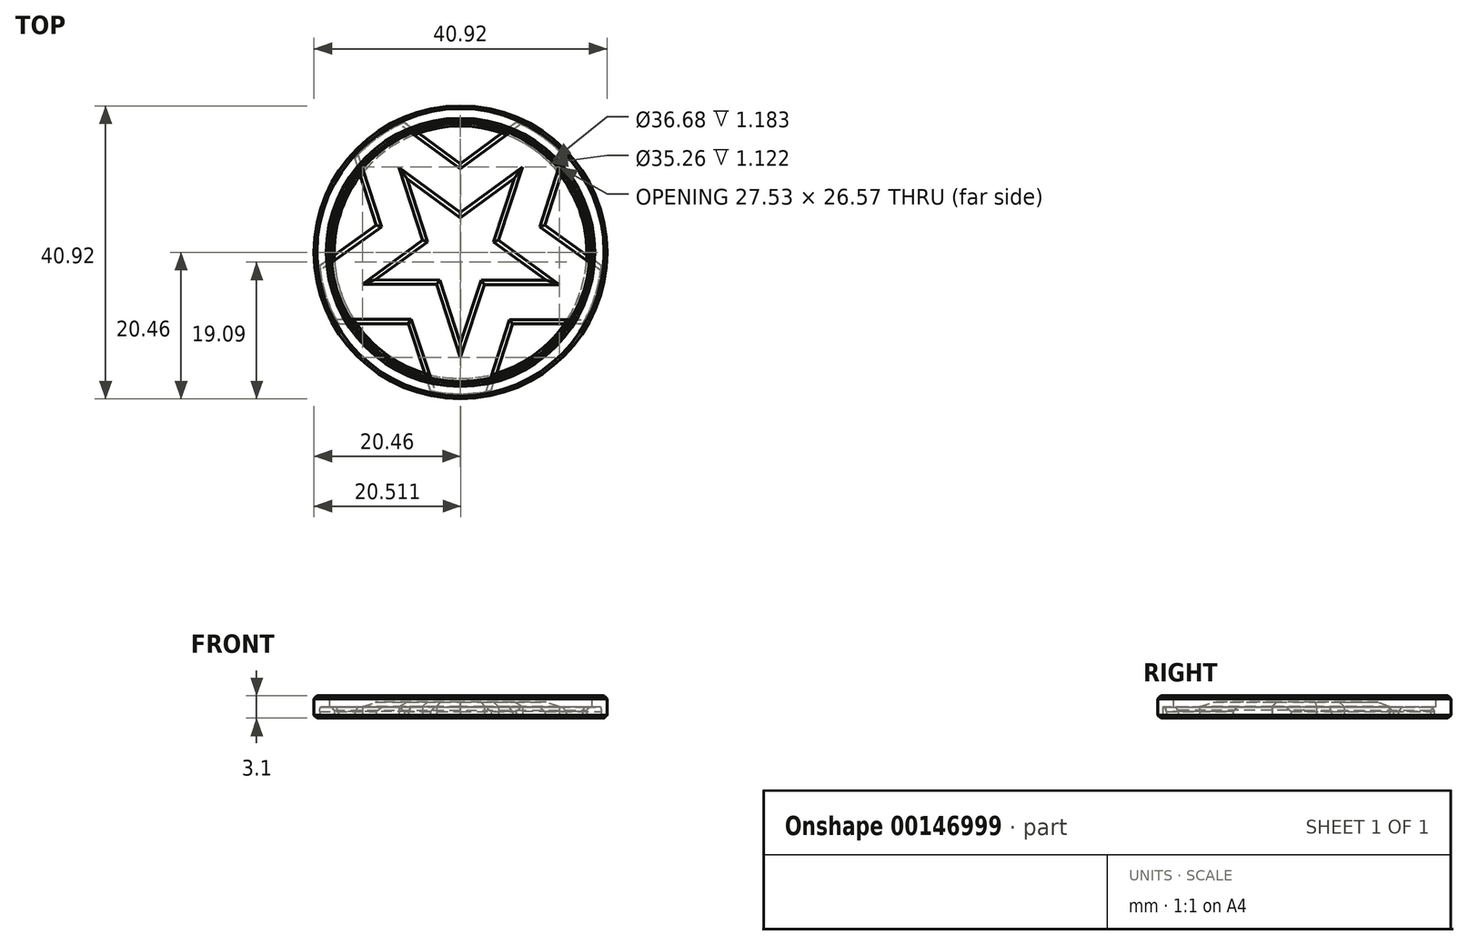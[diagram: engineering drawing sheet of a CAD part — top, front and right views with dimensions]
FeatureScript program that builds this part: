
annotation { "Feature Type Name" : "Feature", "Feature Type Description" : "" }
export const myFeature = defineFeature(function(context is Context, id is Id, definition is map)
    precondition{}
    {
        {
            var Q0;
            Q0=qCreatedBy(makeId("Front.planeOp"),FACE);
            var sketch = newSketch(context, id + "F0", { "sketchPlane" : qUnion([Q0])});
            skLineSegment(sketch, "E0", {"start": v(0, 0) * mm, "end": v(0, 30.47) * mm});
            skSolve(sketch);
        }
        {
            var Q0;
            Q0=qCreatedBy(makeId("Front.planeOp"),FACE);
            var sketch = newSketch(context, id + "F1", { "sketchPlane" : qUnion([Q0])});
            skLineSegment(sketch, "E1", {"start": v(20.46, -1.5) * mm, "end": v(20.46, 1.61) * mm});
            skLineSegment(sketch, "E2", {"start": v(20.46, -1.5) * mm, "end": v(17.63, -1.5) * mm});
            skLineSegment(sketch, "E3.MirrorCS", {"start": v(20.46, 1.61) * mm, "end": v(18.34, 1.61) * mm});
            skPoint(sketch, "E4.orphan", {"position": v(18.34, -0.8) * mm});
            skLineSegment(sketch, "E5", {"start": v(18.34, 0.03) * mm, "end": v(17.63, 0.03) * mm});
            skLineSegment(sketch, "E6", {"start": v(17.63, 0.03) * mm, "end": v(17.63, -1.5) * mm});
            skPoint(sketch, "E7.orphan", {"position": v(18.98, -1.65) * mm});
            skPoint(sketch, "E8.end.orphan", {"position": v(18.34, -1.45) * mm});
            skPoint(sketch, "E9.orphan", {"position": v(17.63, -1.65) * mm});
            skLineSegment(sketch, "E10", {"start": v(18.34, 1.61) * mm, "end": v(18.34, 0.03) * mm});
            skSolve(sketch);
        }
        {
            var Q0;
            Q0=makeQuery(id+"F1.imprint","IMPRINT",FACE,{"disambiguationData":[TD([[makeQuery(id+"F1.imprint","IMPRINT",EDGE,{"derivedFrom":sQuery(id+"F1.wireOp",EDGE,"E1")}),1.0]])]});
            var Q1;
            Q1=sQuery(id+"F0.wireOp",EDGE,"E0");
            revolve(context, id + "F2", {"entities" : qUnion([Q0]), "axis" : qUnion([Q1]), "revolveType" : RevolveType.FULL});
        }
        {
            var Q0;
            Q0=qCreatedBy(makeId("Top.planeOp"),FACE);
            var sketch = newSketch(context, id + "F3", { "sketchPlane" : qUnion([Q0])});
            skLineSegment(sketch, "E11", {"start": v(-14.78, 13.1) * mm, "end": v(-11.75, 3.8) * mm});
            skLineSegment(sketch, "E12", {"start": v(-11.75, 3.8) * mm, "end": v(-19.67, -1.86) * mm});
            skLineSegment(sketch, "E13", {"start": v(-17.05, -9.97) * mm, "end": v(-7.3, -9.97) * mm});
            skLineSegment(sketch, "E14", {"start": v(-7.3, -9.97) * mm, "end": v(-4.23, -19.3) * mm});
            skLineSegment(sketch, "E15", {"start": v(4.27, -19.29) * mm, "end": v(7.28, -10.01) * mm});
            skLineSegment(sketch, "E16", {"start": v(7.28, -10.01) * mm, "end": v(17.03, -10.01) * mm});
            skLineSegment(sketch, "E17", {"start": v(19.67, -1.87) * mm, "end": v(11.78, 3.78) * mm});
            skLineSegment(sketch, "E18", {"start": v(11.78, 3.78) * mm, "end": v(14.76, 13.13) * mm});
            skLineSegment(sketch, "E19", {"start": v(7.81, 18.15) * mm, "end": v(0, 12.4) * mm});
            skLineSegment(sketch, "E20", {"start": v(0, 12.4) * mm, "end": v(-7.85, 18.13) * mm});
            skArc(sketch, "E21", {"start": v(-19.67, -1.86) * mm, "mid": v(-18.8, -6.06) * mm, "end": v(-17.05, -9.97) * mm});
            skArc(sketch, "E22.trimOffspring", {"start": v(-4.23, -19.3) * mm, "mid": v(0.02, -19.76) * mm, "end": v(4.27, -19.29) * mm});
            skArc(sketch, "E23.trimOffspring", {"start": v(17.03, -10.01) * mm, "mid": v(18.8, -6.09) * mm, "end": v(19.67, -1.87) * mm});
            skArc(sketch, "E24.trimOffspring", {"start": v(14.76, 13.13) * mm, "mid": v(11.56, 16.02) * mm, "end": v(7.81, 18.15) * mm});
            skArc(sketch, "E25.trimOffspring", {"start": v(-7.85, 18.13) * mm, "mid": v(-11.6, 16) * mm, "end": v(-14.78, 13.1) * mm});
            skSolve(sketch);
        }
        {
            var Q0;
            Q0=makeQuery(id+"F3.imprint","IMPRINT",FACE,{"disambiguationData":[TD([[makeQuery(id+"F3.imprint","IMPRINT",EDGE,{"derivedFrom":sQuery(id+"F3.wireOp",EDGE,"E11")}),1.0]])]});
            extrude(context, id + "F4", {"entities" : qUnion([Q0]), "endBound" : BoundingType.SYMMETRIC, "depth" : 1.4 * mm});
        }
        {
            var Q0;
            Q0=qCreatedBy(makeId("Top.planeOp"),FACE);
            var sketch = newSketch(context, id + "F5", { "sketchPlane" : qUnion([Q0])});
            skLineSegment(sketch, "E26.0", {"start": v(-5.73, 7.9) * mm, "end": v(0, 3.72) * mm});
            skLineSegment(sketch, "E26.1", {"start": v(-9.14, -2.97) * mm, "end": v(-3.53, 1.13) * mm});
            skLineSegment(sketch, "E26.2", {"start": v(5.78, 7.94) * mm, "end": v(3.55, 1.12) * mm});
            skLineSegment(sketch, "E26.3", {"start": v(9.21, -3.02) * mm, "end": v(2.2, -3) * mm});
            skLineSegment(sketch, "E26.4", {"start": v(0, -9.77) * mm, "end": v(-2.2, -2.99) * mm});
            skLineSegment(sketch, "E27.trimOffspring", {"start": v(2.2, -3) * mm, "end": v(0, -9.77) * mm});
            skLineSegment(sketch, "E28.trimOffspring", {"start": v(3.55, 1.12) * mm, "end": v(9.21, -3.02) * mm});
            skLineSegment(sketch, "E29.trimOffspring", {"start": v(-2.2, -2.99) * mm, "end": v(-9.14, -2.97) * mm});
            skLineSegment(sketch, "E30.trimOffspring", {"start": v(0, 3.72) * mm, "end": v(5.78, 7.94) * mm});
            skLineSegment(sketch, "E31.trimOffspring", {"start": v(-3.53, 1.13) * mm, "end": v(-5.73, 7.9) * mm});
            skSolve(sketch);
        }
        {
            var Q0;
            Q0=makeQuery(id+"F5.imprint","IMPRINT",FACE,{"disambiguationData":[TD([[makeQuery(id+"F5.imprint","IMPRINT",EDGE,{"derivedFrom":sQuery(id+"F5.wireOp",EDGE,"E26.0")}),-1.0]])]});
            extrude(context, id + "F6", {"entities" : qUnion([Q0]), "endBound" : BoundingType.SYMMETRIC, "depth" : 1.4 * mm});
        }
        {
            var Q0;
            Q0=makeQuery(id+"F6.opExtrude","SWEPT_BODY",BODY,{"disambiguationData":[OSD([sQuery(id+"F5.wireOp",EDGE,"E26.0"),sQuery(id+"F5.wireOp",EDGE,"E26.1"),sQuery(id+"F5.wireOp",EDGE,"E26.2"),sQuery(id+"F5.wireOp",EDGE,"E26.3"),sQuery(id+"F5.wireOp",EDGE,"E26.4"),sQuery(id+"F5.wireOp",EDGE,"E27.trimOffspring"),sQuery(id+"F5.wireOp",EDGE,"E28.trimOffspring"),sQuery(id+"F5.wireOp",EDGE,"E29.trimOffspring"),sQuery(id+"F5.wireOp",EDGE,"E30.trimOffspring"),sQuery(id+"F5.wireOp",EDGE,"E31.trimOffspring")])]});
            var Q1;
            Q1=qCreatedBy(makeId("Origin.pointOp"),VERTEX);
            transform(context, id + "F7", {"entities" : qUnion([Q0]), "transformType" : TransformType.SCALE_UNIFORMLY, "scale" : 1.5, "scalePoint" : qUnion([Q1]), "makeCopy" : false});
        }
        {
            var Q0;
            Q0=makeQuery(id+"F4.opExtrude","SWEPT_BODY",BODY,{"disambiguationData":[OSD([sQuery(id+"F3.wireOp",EDGE,"E11"),sQuery(id+"F3.wireOp",EDGE,"E12"),sQuery(id+"F3.wireOp",EDGE,"E13"),sQuery(id+"F3.wireOp",EDGE,"E14"),sQuery(id+"F3.wireOp",EDGE,"E15"),sQuery(id+"F3.wireOp",EDGE,"E16"),sQuery(id+"F3.wireOp",EDGE,"E17"),sQuery(id+"F3.wireOp",EDGE,"E18"),sQuery(id+"F3.wireOp",EDGE,"E19"),sQuery(id+"F3.wireOp",EDGE,"E20"),sQuery(id+"F3.wireOp",EDGE,"E21"),sQuery(id+"F3.wireOp",EDGE,"E22.trimOffspring"),sQuery(id+"F3.wireOp",EDGE,"E23.trimOffspring"),sQuery(id+"F3.wireOp",EDGE,"E24.trimOffspring"),sQuery(id+"F3.wireOp",EDGE,"E25.trimOffspring")])]});
            transform(context, id + "F8", {"entities" : qUnion([Q0]), "transformType" : TransformType.TRANSLATION_3D, "dx" : 0 * mm, "dy" : 0 * mm, "dz" : -1 * mm, "makeCopy" : false});
        }
        {
            var Q0;
            Q0=makeQuery(id+"F6.opExtrude","SWEPT_BODY",BODY,{"disambiguationData":[OSD([sQuery(id+"F5.wireOp",EDGE,"E26.0"),sQuery(id+"F5.wireOp",EDGE,"E26.1"),sQuery(id+"F5.wireOp",EDGE,"E26.2"),sQuery(id+"F5.wireOp",EDGE,"E26.3"),sQuery(id+"F5.wireOp",EDGE,"E26.4"),sQuery(id+"F5.wireOp",EDGE,"E27.trimOffspring"),sQuery(id+"F5.wireOp",EDGE,"E28.trimOffspring"),sQuery(id+"F5.wireOp",EDGE,"E29.trimOffspring"),sQuery(id+"F5.wireOp",EDGE,"E30.trimOffspring"),sQuery(id+"F5.wireOp",EDGE,"E31.trimOffspring")])]});
            transform(context, id + "F9", {"entities" : qUnion([Q0]), "transformType" : TransformType.TRANSLATION_3D, "dx" : 0 * mm, "dy" : 0 * mm, "dz" : -0.5 * mm, "makeCopy" : false});
        }
        {
            var Q0;
            Q0=makeQuery(id+"F4.opExtrude","SWEPT_BODY",BODY,{"disambiguationData":[OSD([sQuery(id+"F3.wireOp",EDGE,"E11"),sQuery(id+"F3.wireOp",EDGE,"E12"),sQuery(id+"F3.wireOp",EDGE,"E13"),sQuery(id+"F3.wireOp",EDGE,"E14"),sQuery(id+"F3.wireOp",EDGE,"E15"),sQuery(id+"F3.wireOp",EDGE,"E16"),sQuery(id+"F3.wireOp",EDGE,"E17"),sQuery(id+"F3.wireOp",EDGE,"E18"),sQuery(id+"F3.wireOp",EDGE,"E19"),sQuery(id+"F3.wireOp",EDGE,"E20"),sQuery(id+"F3.wireOp",EDGE,"E21"),sQuery(id+"F3.wireOp",EDGE,"E22.trimOffspring"),sQuery(id+"F3.wireOp",EDGE,"E23.trimOffspring"),sQuery(id+"F3.wireOp",EDGE,"E24.trimOffspring"),sQuery(id+"F3.wireOp",EDGE,"E25.trimOffspring")])]});
            transform(context, id + "F10", {"entities" : qUnion([Q0]), "transformType" : TransformType.TRANSLATION_3D, "dx" : 0 * mm, "dy" : 0 * mm, "dz" : 0.2 * mm, "makeCopy" : false});
        }
        {
            var Q0;
            Q0=makeQuery(id+"F6.opExtrude","SWEPT_BODY",BODY,{"disambiguationData":[OSD([sQuery(id+"F5.wireOp",EDGE,"E26.0"),sQuery(id+"F5.wireOp",EDGE,"E26.1"),sQuery(id+"F5.wireOp",EDGE,"E26.2"),sQuery(id+"F5.wireOp",EDGE,"E26.3"),sQuery(id+"F5.wireOp",EDGE,"E26.4"),sQuery(id+"F5.wireOp",EDGE,"E27.trimOffspring"),sQuery(id+"F5.wireOp",EDGE,"E28.trimOffspring"),sQuery(id+"F5.wireOp",EDGE,"E29.trimOffspring"),sQuery(id+"F5.wireOp",EDGE,"E30.trimOffspring"),sQuery(id+"F5.wireOp",EDGE,"E31.trimOffspring")])]});
            transform(context, id + "F11", {"entities" : qUnion([Q0]), "transformType" : TransformType.TRANSLATION_3D, "dx" : 0 * mm, "dy" : 0 * mm, "dz" : 0.2 * mm, "makeCopy" : false});
        }
        {
            var Q0;
            Q0=makeQuery(id+"F4.opExtrude","CAP_EDGE",EDGE,{"disambiguationData":[OSD([sQuery(id+"F3.wireOp",EDGE,"E17")])],"isStart":false});
            var Q1;
            Q1=makeQuery(id+"F4.opExtrude","CAP_EDGE",EDGE,{"disambiguationData":[OSD([sQuery(id+"F3.wireOp",EDGE,"E18")])],"isStart":false});
            var Q2;
            Q2=makeQuery(id+"F4.opExtrude","CAP_EDGE",EDGE,{"disambiguationData":[OSD([sQuery(id+"F3.wireOp",EDGE,"E19")])],"isStart":false});
            var Q3;
            Q3=makeQuery(id+"F4.opExtrude","CAP_EDGE",EDGE,{"disambiguationData":[OSD([sQuery(id+"F3.wireOp",EDGE,"E20")])],"isStart":false});
            var Q4;
            Q4=makeQuery(id+"F4.opExtrude","CAP_EDGE",EDGE,{"disambiguationData":[OSD([sQuery(id+"F3.wireOp",EDGE,"E11")])],"isStart":false});
            var Q5;
            Q5=makeQuery(id+"F4.opExtrude","CAP_EDGE",EDGE,{"disambiguationData":[OSD([sQuery(id+"F3.wireOp",EDGE,"E12")])],"isStart":false});
            var Q6;
            Q6=makeQuery(id+"F4.opExtrude","CAP_EDGE",EDGE,{"disambiguationData":[OSD([sQuery(id+"F3.wireOp",EDGE,"E13")])],"isStart":false});
            var Q7;
            Q7=makeQuery(id+"F4.opExtrude","CAP_EDGE",EDGE,{"disambiguationData":[OSD([sQuery(id+"F3.wireOp",EDGE,"E14")])],"isStart":false});
            var Q8;
            Q8=makeQuery(id+"F4.opExtrude","CAP_EDGE",EDGE,{"disambiguationData":[OSD([sQuery(id+"F3.wireOp",EDGE,"E15")])],"isStart":false});
            var Q9;
            Q9=makeQuery(id+"F4.opExtrude","CAP_EDGE",EDGE,{"disambiguationData":[OSD([sQuery(id+"F3.wireOp",EDGE,"E16")])],"isStart":false});
            var Q10;
            Q10=makeQuery(id+"F6.opExtrude","CAP_FACE",FACE,{"disambiguationData":[OSD([sQuery(id+"F5.wireOp",EDGE,"E26.0"),sQuery(id+"F5.wireOp",EDGE,"E26.1"),sQuery(id+"F5.wireOp",EDGE,"E26.2"),sQuery(id+"F5.wireOp",EDGE,"E26.3"),sQuery(id+"F5.wireOp",EDGE,"E26.4"),sQuery(id+"F5.wireOp",EDGE,"E27.trimOffspring"),sQuery(id+"F5.wireOp",EDGE,"E28.trimOffspring"),sQuery(id+"F5.wireOp",EDGE,"E29.trimOffspring"),sQuery(id+"F5.wireOp",EDGE,"E30.trimOffspring"),sQuery(id+"F5.wireOp",EDGE,"E31.trimOffspring")])],"isStart":false});
            chamfer(context, id + "F12", {"entities" : qUnion([Q0, Q1, Q2, Q3, Q4, Q5, Q6, Q7, Q8, Q9, Q10]), "chamferType" : ChamferType.OFFSET_ANGLE, "width" : .6 * mm, "oppositeDirection" : false, "angle" : 45 * degree});
        }
        {
            var Q0;
            Q0=makeQuery(id+"F2.opRevolve","SWEPT_EDGE",EDGE,{"disambiguationData":[OSD([sQuery(id+"F1.wireOp",EDGE,"E5"),sQuery(id+"F1.wireOp",EDGE,"E6")])]});
            chamfer(context, id + "F13", {"entities" : qUnion([Q0]), "width" : .4 * mm, "tangentPropagation" : true});
        }
        {
            var Q0;
            Q0=makeQuery(id+"F2.opRevolve","SWEPT_FACE",FACE,{"disambiguationData":[OSD([sQuery(id+"F1.wireOp",EDGE,"E3.MirrorCS")])]});
            chamfer(context, id + "F14", {"entities" : qUnion([Q0]), "width" : .4 * mm, "tangentPropagation" : true});
        }
        {
            var Q0;
            Q0=makeQuery(id+"F4.opExtrude","SWEPT_BODY",BODY,{"disambiguationData":[OSD([sQuery(id+"F3.wireOp",EDGE,"E11"),sQuery(id+"F3.wireOp",EDGE,"E12"),sQuery(id+"F3.wireOp",EDGE,"E13"),sQuery(id+"F3.wireOp",EDGE,"E14"),sQuery(id+"F3.wireOp",EDGE,"E15"),sQuery(id+"F3.wireOp",EDGE,"E16"),sQuery(id+"F3.wireOp",EDGE,"E17"),sQuery(id+"F3.wireOp",EDGE,"E18"),sQuery(id+"F3.wireOp",EDGE,"E19"),sQuery(id+"F3.wireOp",EDGE,"E20"),sQuery(id+"F3.wireOp",EDGE,"E21"),sQuery(id+"F3.wireOp",EDGE,"E22.trimOffspring"),sQuery(id+"F3.wireOp",EDGE,"E23.trimOffspring"),sQuery(id+"F3.wireOp",EDGE,"E24.trimOffspring"),sQuery(id+"F3.wireOp",EDGE,"E25.trimOffspring")])]});
            transform(context, id + "F15", {"entities" : qUnion([Q0]), "transformType" : TransformType.TRANSLATION_3D, "dx" : 0 * mm, "dy" : 0 * mm, "dz" : 0.02 * mm, "makeCopy" : false});
        }
        {
            var Q0;
            Q0=makeQuery(id+"F2.opRevolve","SWEPT_EDGE",EDGE,{"disambiguationData":[OSD([sQuery(id+"F1.wireOp",EDGE,"E1"),sQuery(id+"F1.wireOp",EDGE,"E2")])]});
            chamfer(context, id + "F16", {"entities" : qUnion([Q0]), "width" : .4 * mm, "tangentPropagation" : true});
        }
        {
            var Q0;
            Q0=makeQuery(id+"F4.opExtrude","SWEPT_BODY",BODY,{"disambiguationData":[OSD([sQuery(id+"F3.wireOp",EDGE,"E11"),sQuery(id+"F3.wireOp",EDGE,"E12"),sQuery(id+"F3.wireOp",EDGE,"E13"),sQuery(id+"F3.wireOp",EDGE,"E14"),sQuery(id+"F3.wireOp",EDGE,"E15"),sQuery(id+"F3.wireOp",EDGE,"E16"),sQuery(id+"F3.wireOp",EDGE,"E17"),sQuery(id+"F3.wireOp",EDGE,"E18"),sQuery(id+"F3.wireOp",EDGE,"E19"),sQuery(id+"F3.wireOp",EDGE,"E20"),sQuery(id+"F3.wireOp",EDGE,"E21"),sQuery(id+"F3.wireOp",EDGE,"E22.trimOffspring"),sQuery(id+"F3.wireOp",EDGE,"E23.trimOffspring"),sQuery(id+"F3.wireOp",EDGE,"E24.trimOffspring"),sQuery(id+"F3.wireOp",EDGE,"E25.trimOffspring")])]});
            transform(context, id + "F17", {"entities" : qUnion([Q0]), "transformType" : TransformType.TRANSLATION_3D, "dx" : 0 * mm, "dy" : 0 * mm, "dz" : 0.1 * mm, "makeCopy" : false});
        }
        {
            var Q0;
            Q0=makeQuery(id+"F6.opExtrude","SWEPT_BODY",BODY,{"disambiguationData":[OSD([sQuery(id+"F5.wireOp",EDGE,"E26.0"),sQuery(id+"F5.wireOp",EDGE,"E26.1"),sQuery(id+"F5.wireOp",EDGE,"E26.2"),sQuery(id+"F5.wireOp",EDGE,"E26.3"),sQuery(id+"F5.wireOp",EDGE,"E26.4"),sQuery(id+"F5.wireOp",EDGE,"E27.trimOffspring"),sQuery(id+"F5.wireOp",EDGE,"E28.trimOffspring"),sQuery(id+"F5.wireOp",EDGE,"E29.trimOffspring"),sQuery(id+"F5.wireOp",EDGE,"E30.trimOffspring"),sQuery(id+"F5.wireOp",EDGE,"E31.trimOffspring")])]});
            transform(context, id + "F18", {"entities" : qUnion([Q0]), "transformType" : TransformType.TRANSLATION_3D, "dx" : 0 * mm, "dy" : 0 * mm, "dz" : -0.03 * mm, "makeCopy" : false});
        }
        {
            var Q0;
            Q0=makeQuery(id+"F6.opExtrude","SWEPT_BODY",BODY,{"disambiguationData":[OSD([sQuery(id+"F5.wireOp",EDGE,"E26.0"),sQuery(id+"F5.wireOp",EDGE,"E26.1"),sQuery(id+"F5.wireOp",EDGE,"E26.2"),sQuery(id+"F5.wireOp",EDGE,"E26.3"),sQuery(id+"F5.wireOp",EDGE,"E26.4"),sQuery(id+"F5.wireOp",EDGE,"E27.trimOffspring"),sQuery(id+"F5.wireOp",EDGE,"E28.trimOffspring"),sQuery(id+"F5.wireOp",EDGE,"E29.trimOffspring"),sQuery(id+"F5.wireOp",EDGE,"E30.trimOffspring"),sQuery(id+"F5.wireOp",EDGE,"E31.trimOffspring")])]});
            transform(context, id + "F19", {"entities" : qUnion([Q0]), "transformType" : TransformType.TRANSLATION_3D, "dx" : 0 * mm, "dy" : 0 * mm, "dz" : 0 * mm, "makeCopy" : true});
        }
        {
            var Q0;
            Q0=makeQuery(id+"F6.opExtrude","SWEPT_BODY",BODY,{"disambiguationData":[OSD([sQuery(id+"F5.wireOp",EDGE,"E26.0"),sQuery(id+"F5.wireOp",EDGE,"E26.1"),sQuery(id+"F5.wireOp",EDGE,"E26.2"),sQuery(id+"F5.wireOp",EDGE,"E26.3"),sQuery(id+"F5.wireOp",EDGE,"E26.4"),sQuery(id+"F5.wireOp",EDGE,"E27.trimOffspring"),sQuery(id+"F5.wireOp",EDGE,"E28.trimOffspring"),sQuery(id+"F5.wireOp",EDGE,"E29.trimOffspring"),sQuery(id+"F5.wireOp",EDGE,"E30.trimOffspring"),sQuery(id+"F5.wireOp",EDGE,"E31.trimOffspring")])]});
            var Q1;
            Q1=makeQuery(id+"F4.opExtrude","SWEPT_BODY",BODY,{"disambiguationData":[OSD([sQuery(id+"F3.wireOp",EDGE,"E11"),sQuery(id+"F3.wireOp",EDGE,"E12"),sQuery(id+"F3.wireOp",EDGE,"E13"),sQuery(id+"F3.wireOp",EDGE,"E14"),sQuery(id+"F3.wireOp",EDGE,"E15"),sQuery(id+"F3.wireOp",EDGE,"E16"),sQuery(id+"F3.wireOp",EDGE,"E17"),sQuery(id+"F3.wireOp",EDGE,"E18"),sQuery(id+"F3.wireOp",EDGE,"E19"),sQuery(id+"F3.wireOp",EDGE,"E20"),sQuery(id+"F3.wireOp",EDGE,"E21"),sQuery(id+"F3.wireOp",EDGE,"E22.trimOffspring"),sQuery(id+"F3.wireOp",EDGE,"E23.trimOffspring"),sQuery(id+"F3.wireOp",EDGE,"E24.trimOffspring"),sQuery(id+"F3.wireOp",EDGE,"E25.trimOffspring")])]});
            booleanBodies(context, id + "F20", {"operationType" : BooleanOperationType.SUBTRACTION, "tools" : qUnion([Q0]), "targets" : qUnion([Q1])});
        }
    });
